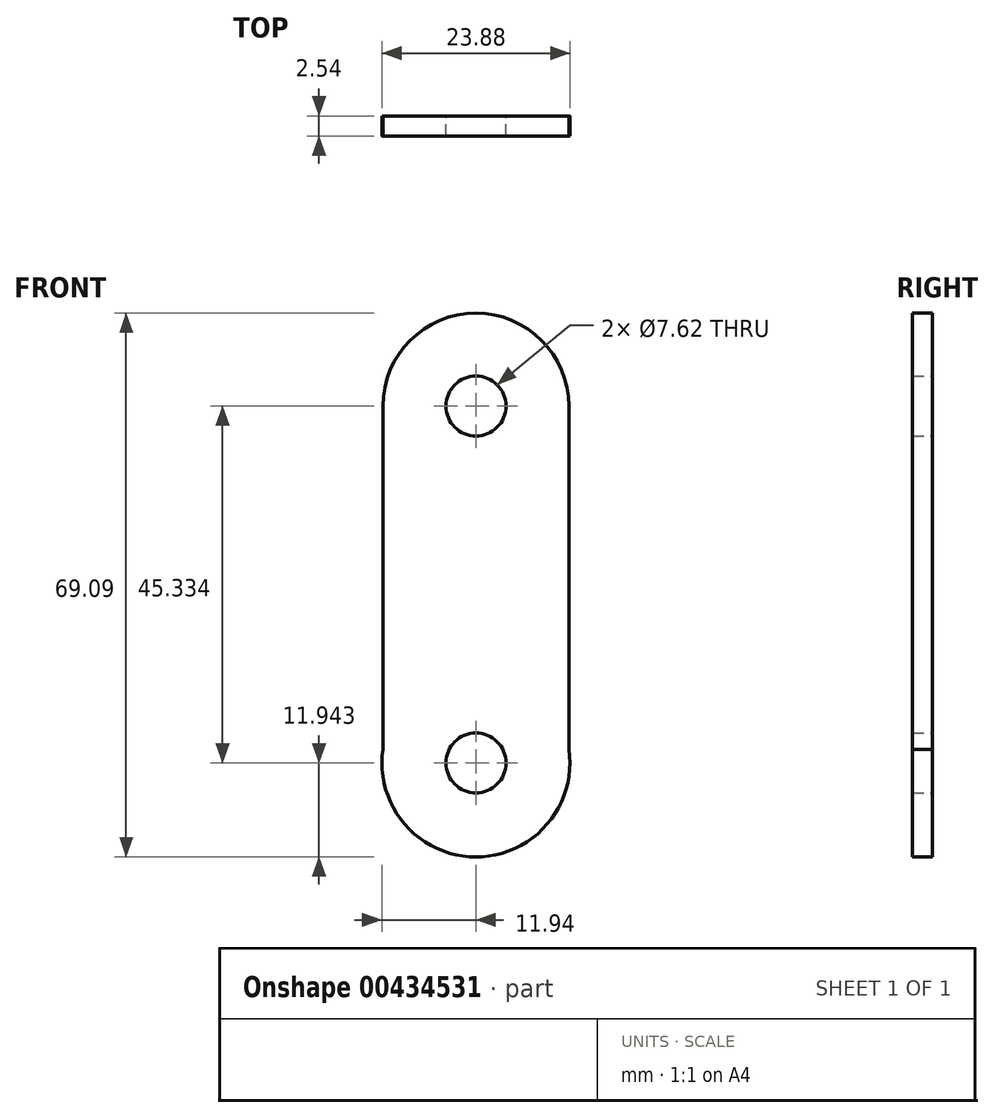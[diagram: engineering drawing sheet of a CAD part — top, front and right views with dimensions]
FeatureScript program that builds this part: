
annotation { "Feature Type Name" : "Feature", "Feature Type Description" : "" }
export const myFeature = defineFeature(function(context is Context, id is Id, definition is map)
    precondition{}
    {
        {
            var Q0;
            Q0=qCreatedBy(makeId("Front.planeOp"),FACE);
            var sketch = newSketch(context, id + "F0", { "sketchPlane" : qUnion([Q0])});
            skLineSegment(sketch, "E0.left", {"start": v(-11.81, 22.67) * mm, "end": v(-11.81, -22.67) * mm});
            skLineSegment(sketch, "E0.right", {"start": v(11.81, 22.67) * mm, "end": v(11.81, -22.67) * mm});
            skPoint(sketch, "E0.middle", {"position": v(0, 0) * mm});
            skArc(sketch, "E1", {"start": v(11.81, 22.67) * mm, "mid": v(0, 34.48) * mm, "end": v(-11.81, 22.67) * mm});
            skArc(sketch, "E2", {"start": v(-11.81, -20.93) * mm, "mid": v(0, -34.6) * mm, "end": v(11.81, -20.93) * mm});
            skCircle(sketch, "E3", {"center": v(0, -22.67) * mm, "radius": 3.81 * mm});
            skCircle(sketch, "E4", {"center": v(0, 22.67) * mm, "radius": 3.8 * mm});
            skSolve(sketch);
        }
        {
            var Q0;
            Q0 = qSketchRegion(id + "F0", true);
            extrude(context, id + "F1", {"entities" : qUnion([Q0]), "depth" : 2.54 * mm});
        }
    });
